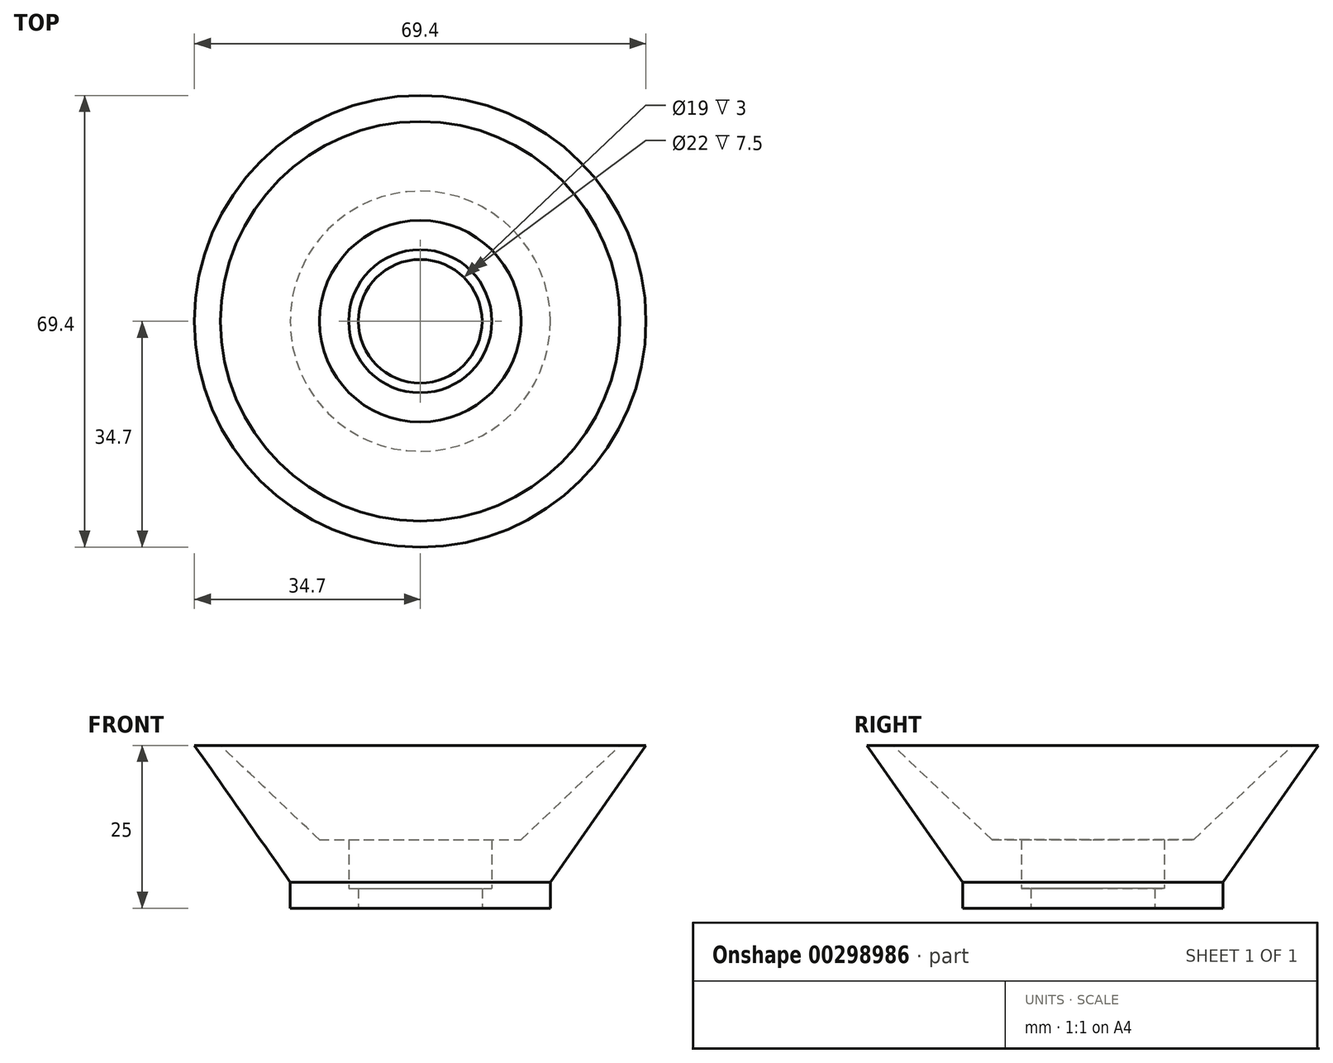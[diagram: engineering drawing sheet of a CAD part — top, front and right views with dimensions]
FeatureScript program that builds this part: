
annotation { "Feature Type Name" : "Feature", "Feature Type Description" : "" }
export const myFeature = defineFeature(function(context is Context, id is Id, definition is map)
    precondition{}
    {
        {
            var Q0;
            Q0=qCreatedBy(makeId("Front.planeOp"),FACE);
            var sketch = newSketch(context, id + "F0", { "sketchPlane" : qUnion([Q0])});
            skLineSegment(sketch, "E0", {"start": v(9.5, 0) * mm, "end": v(9.5, 3) * mm});
            skLineSegment(sketch, "E1", {"start": v(9.5, 3) * mm, "end": v(11, 3) * mm});
            skLineSegment(sketch, "E2", {"start": v(11, 3) * mm, "end": v(11, 10.5) * mm});
            skLineSegment(sketch, "E3", {"start": v(11, 10.5) * mm, "end": v(15.5, 10.5) * mm});
            skLineSegment(sketch, "E4", {"start": v(15.5, 10.5) * mm, "end": v(30.7, 25) * mm});
            skLineSegment(sketch, "E5", {"start": v(30.7, 25) * mm, "end": v(34.7, 25) * mm});
            skLineSegment(sketch, "E6", {"start": v(34.7, 25) * mm, "end": v(20, 4) * mm});
            skLineSegment(sketch, "E7", {"start": v(20, 4) * mm, "end": v(20, 0) * mm});
            skLineSegment(sketch, "E8", {"start": v(20, 0) * mm, "end": v(9.5, 0) * mm});
            skLineSegment(sketch, "E9", {"start": v(0, 0) * mm, "end": v(0, 60.44) * mm, "construction": true});
            skSolve(sketch);
        }
        {
            var Q0;
            Q0 = qSketchRegion(id + "F0", true);
            var Q1;
            Q1=sQuery(id+"F0.wireOp",EDGE,"E9");
            revolve(context, id + "F1", {"entities" : qUnion([Q0]), "axis" : qUnion([Q1]), "revolveType" : RevolveType.FULL});
        }
    });
